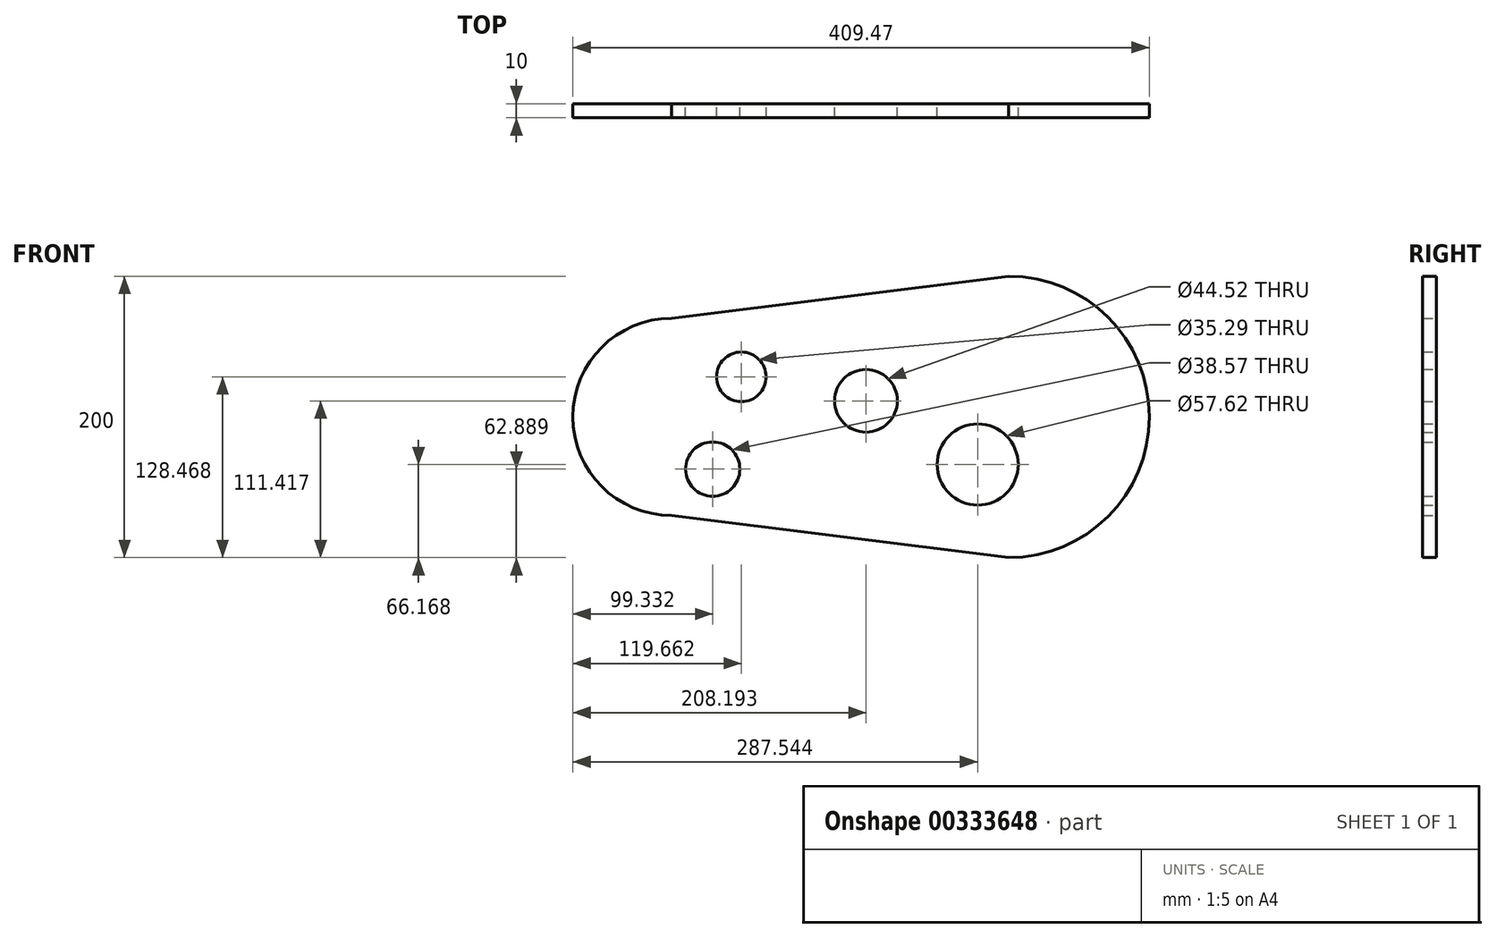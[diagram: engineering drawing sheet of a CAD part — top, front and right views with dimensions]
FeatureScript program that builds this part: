
annotation { "Feature Type Name" : "Feature", "Feature Type Description" : "" }
export const myFeature = defineFeature(function(context is Context, id is Id, definition is map)
    precondition{}
    {
        {
            var Q0;
            Q0=qCreatedBy(makeId("Front.planeOp"),FACE);
            var sketch = newSketch(context, id + "F0", { "sketchPlane" : qUnion([Q0])});
            skArc(sketch, "E0", {"start": v(0, -100) * mm, "mid": v(100, 0) * mm, "end": v(0, 100) * mm});
            skArc(sketch, "E1", {"start": v(-239.47, 70) * mm, "mid": v(-309.47, 0) * mm, "end": v(-239.47, -70) * mm});
            skLineSegment(sketch, "E2", {"start": v(-239.47, 70) * mm, "end": v(0, 100) * mm});
            skLineSegment(sketch, "E3", {"start": v(-239.47, -70) * mm, "end": v(0, -100) * mm});
            skCircle(sketch, "E4", {"center": v(-210.14, -37.11) * mm, "radius": 19.29 * mm});
            skCircle(sketch, "E5", {"center": v(-189.8, 28.47) * mm, "radius": 17.65 * mm});
            skCircle(sketch, "E6", {"center": v(-101.28, 11.42) * mm, "radius": 22.26 * mm});
            skCircle(sketch, "E7", {"center": v(-21.93, -33.83) * mm, "radius": 28.8 * mm});
            skSolve(sketch);
        }
        {
            var Q0;
            Q0 = qSketchRegion(id + "F0", true);
            extrude(context, id + "F1", {"entities" : qUnion([Q0]), "depth" : 10 * mm});
        }
    });
